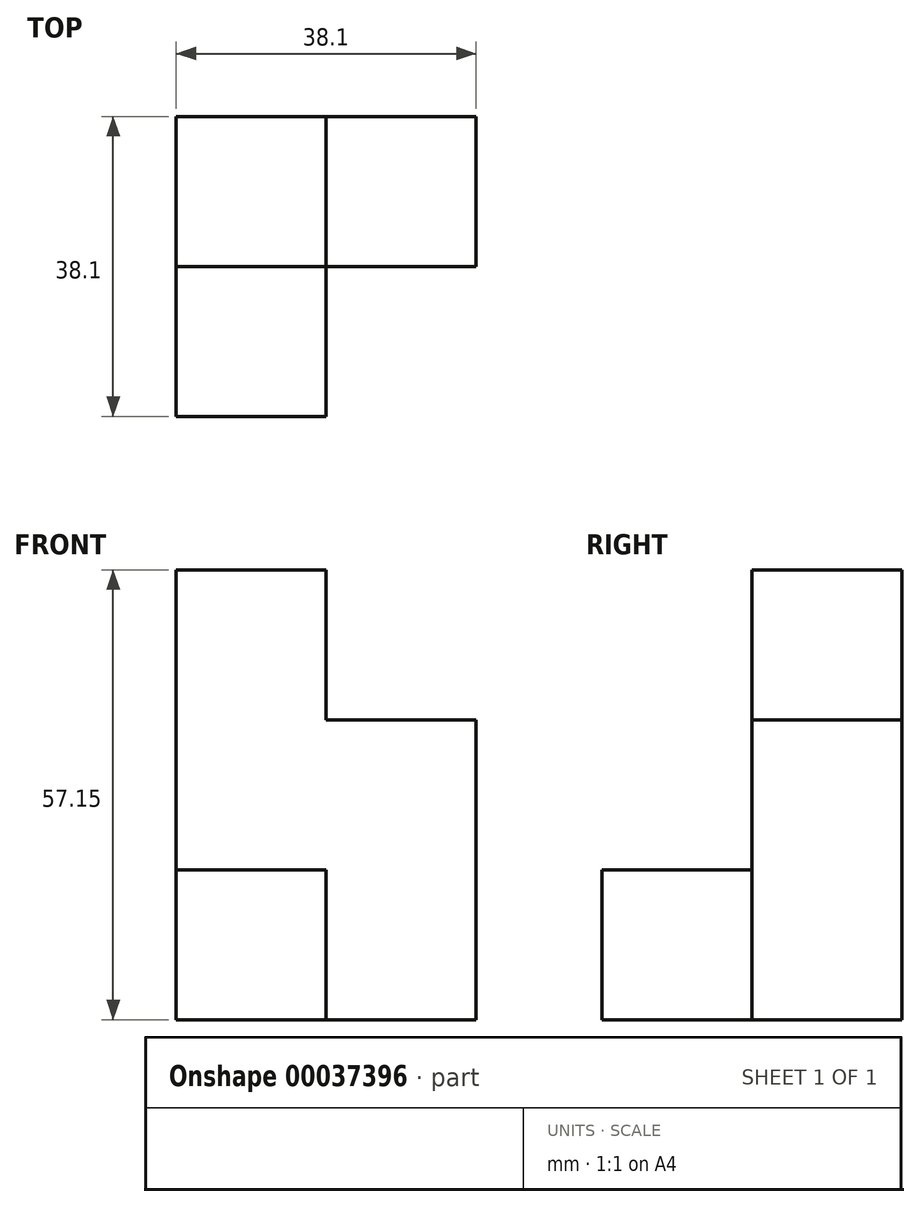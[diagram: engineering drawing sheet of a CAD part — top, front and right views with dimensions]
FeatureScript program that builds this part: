
annotation { "Feature Type Name" : "Feature", "Feature Type Description" : "" }
export const myFeature = defineFeature(function(context is Context, id is Id, definition is map)
    precondition{}
    {
        {
            var Q0;
            Q0=qCreatedBy(makeId("Top.planeOp"),FACE);
            var sketch = newSketch(context, id + "F0", { "sketchPlane" : qUnion([Q0])});
            skLineSegment(sketch, "E0.bottom", {"start": v(0, 0) * mm, "end": v(38.1, 0) * mm});
            skLineSegment(sketch, "E0.top", {"start": v(0, 38.1) * mm, "end": v(38.1, 38.1) * mm});
            skLineSegment(sketch, "E0.left", {"start": v(0, 0) * mm, "end": v(0, 38.1) * mm});
            skLineSegment(sketch, "E0.right", {"start": v(38.1, 0) * mm, "end": v(38.1, 38.1) * mm});
            skSolve(sketch);
        }
        {
            var Q0;
            Q0 = qSketchRegion(id + "F0", true);
            extrude(context, id + "F1", {"entities" : qUnion([Q0]), "depth" : 57.15 * mm});
        }
        {
            var Q0;
            Q0=makeQuery(id+"F1.opExtrude","CAP_FACE",FACE,{"disambiguationData":[OSD([sQuery(id+"F0.wireOp",EDGE,"E0.bottom"),sQuery(id+"F0.wireOp",EDGE,"E0.top"),sQuery(id+"F0.wireOp",EDGE,"E0.left"),sQuery(id+"F0.wireOp",EDGE,"E0.right")])],"isStart":false});
            var sketch = newSketch(context, id + "F2", { "sketchPlane" : qUnion([Q0])});
            skLineSegment(sketch, "E1.bottom", {"start": v(38.1, 0) * mm, "end": v(19.05, 0) * mm});
            skLineSegment(sketch, "E1.top", {"start": v(38.1, 19.05) * mm, "end": v(19.05, 19.05) * mm});
            skLineSegment(sketch, "E1.left", {"start": v(38.1, 0) * mm, "end": v(38.1, 19.05) * mm});
            skLineSegment(sketch, "E1.right", {"start": v(19.05, 0) * mm, "end": v(19.05, 19.05) * mm});
            skSolve(sketch);
        }
        {
            var Q0;
            Q0 = qSketchRegion(id + "F2", true);
            extrude(context, id + "F3", {"entities" : qUnion([Q0]), "operationType" : NewBodyOperationType.REMOVE, "endBound" : BoundingType.THROUGH_ALL, "oppositeDirection" : true, "depth" : 25.4 * mm});
        }
        {
            var Q0;
            Q0=makeQuery(id+"F1.opExtrude","CAP_FACE",FACE,{"disambiguationData":[OSD([sQuery(id+"F0.wireOp",EDGE,"E0.bottom"),sQuery(id+"F0.wireOp",EDGE,"E0.top"),sQuery(id+"F0.wireOp",EDGE,"E0.left"),sQuery(id+"F0.wireOp",EDGE,"E0.right")])],"isStart":false});
            var sketch = newSketch(context, id + "F4", { "sketchPlane" : qUnion([Q0])});
            skLineSegment(sketch, "E2.bottom", {"start": v(19.05, 19.05) * mm, "end": v(38.1, 19.05) * mm});
            skLineSegment(sketch, "E2.top", {"start": v(19.05, 38.1) * mm, "end": v(38.1, 38.1) * mm});
            skLineSegment(sketch, "E2.left", {"start": v(19.05, 19.05) * mm, "end": v(19.05, 38.1) * mm});
            skLineSegment(sketch, "E2.right", {"start": v(38.1, 19.05) * mm, "end": v(38.1, 38.1) * mm});
            skSolve(sketch);
        }
        {
            var Q0;
            Q0 = qSketchRegion(id + "F4", true);
            extrude(context, id + "F5", {"entities" : qUnion([Q0]), "operationType" : NewBodyOperationType.REMOVE, "oppositeDirection" : true, "depth" : 19.05 * mm});
        }
        {
            var Q0;
            Q0=makeQuery(id+"F1.opExtrude","CAP_FACE",FACE,{"disambiguationData":[OSD([sQuery(id+"F0.wireOp",EDGE,"E0.bottom"),sQuery(id+"F0.wireOp",EDGE,"E0.top"),sQuery(id+"F0.wireOp",EDGE,"E0.left"),sQuery(id+"F0.wireOp",EDGE,"E0.right")])],"isStart":false});
            var sketch = newSketch(context, id + "F6", { "sketchPlane" : qUnion([Q0])});
            skLineSegment(sketch, "E3.bottom", {"start": v(0, 0) * mm, "end": v(19.05, 0) * mm});
            skLineSegment(sketch, "E3.top", {"start": v(0, 19.05) * mm, "end": v(19.05, 19.05) * mm});
            skLineSegment(sketch, "E3.left", {"start": v(0, 0) * mm, "end": v(0, 19.05) * mm});
            skLineSegment(sketch, "E3.right", {"start": v(19.05, 0) * mm, "end": v(19.05, 19.05) * mm});
            skSolve(sketch);
        }
        {
            var Q0;
            Q0 = qSketchRegion(id + "F6", true);
            extrude(context, id + "F7", {"entities" : qUnion([Q0]), "operationType" : NewBodyOperationType.REMOVE, "oppositeDirection" : true, "depth" : 38.1 * mm});
        }
    });
